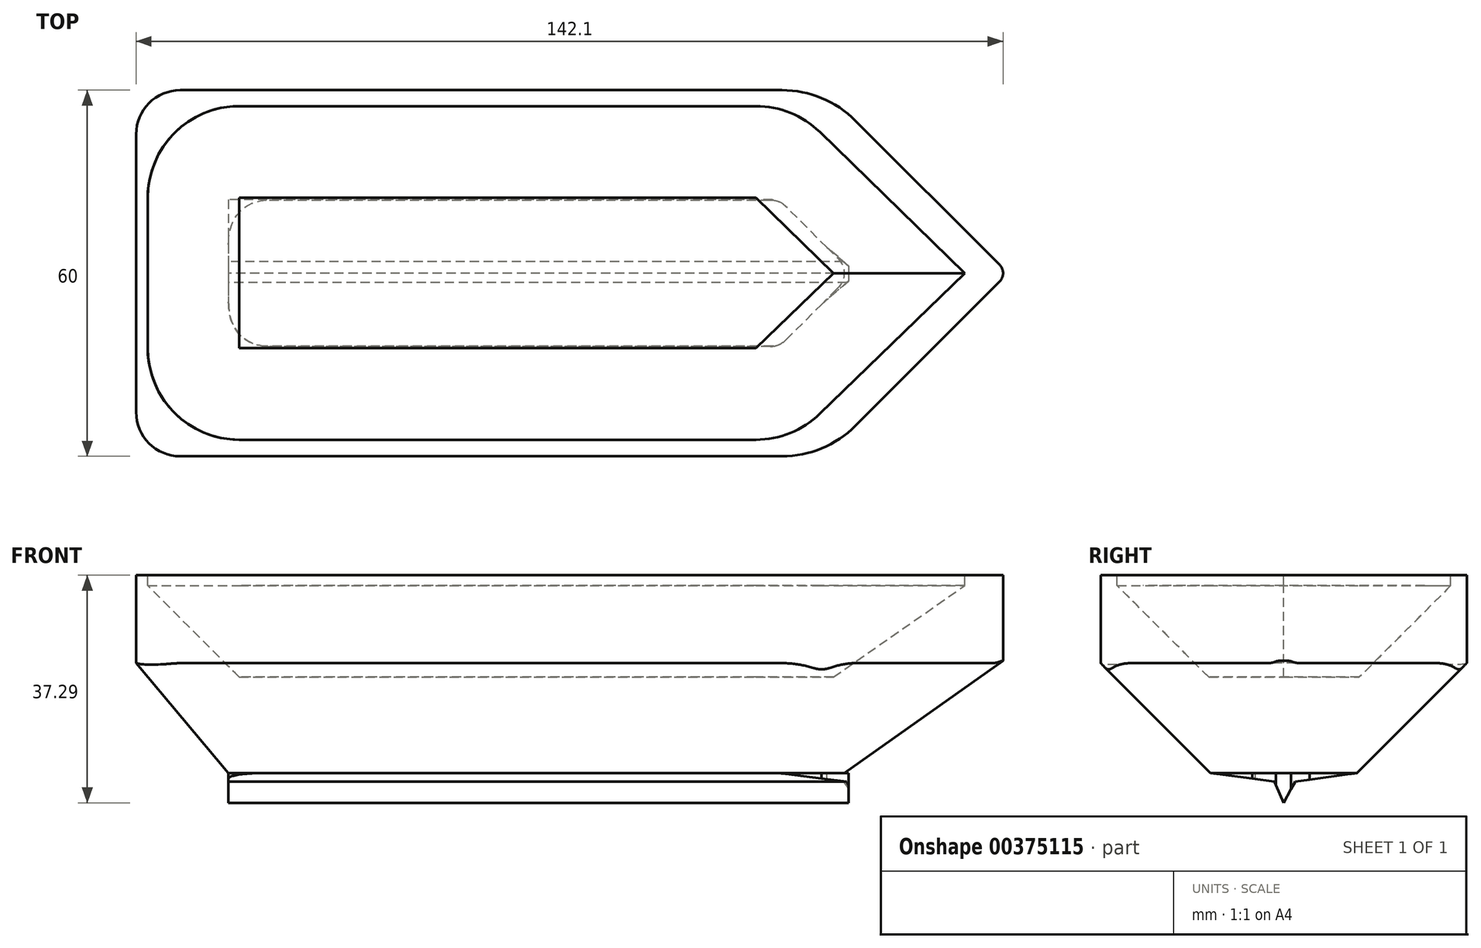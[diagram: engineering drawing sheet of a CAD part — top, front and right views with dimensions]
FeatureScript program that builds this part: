
annotation { "Feature Type Name" : "Feature", "Feature Type Description" : "" }
export const myFeature = defineFeature(function(context is Context, id is Id, definition is map)
    precondition{}
    {
        {
            var Q0;
            Q0=qCreatedBy(makeId("Top.planeOp"),FACE);
            var sketch = newSketch(context, id + "F0", { "sketchPlane" : qUnion([Q0])});
            skLineSegment(sketch, "E0", {"start": v(-55.59, 0) * mm, "end": v(-55.59, 30) * mm});
            skLineSegment(sketch, "E1", {"start": v(-55.59, 30) * mm, "end": v(-55.59, -30) * mm});
            skLineSegment(sketch, "E2", {"start": v(-55.59, -30) * mm, "end": v(87.31, -30) * mm});
            skLineSegment(sketch, "E3", {"start": v(87.31, -30) * mm, "end": v(87.31, 30) * mm});
            skLineSegment(sketch, "E4", {"start": v(87.31, 30) * mm, "end": v(-55.59, 30) * mm});
            skSolve(sketch);
        }
        {
            var Q0;
            {var subQ2=sQuery(id+"F0.wireOp",EDGE,"E2");Q0=makeQuery(id+"F0.imprint","IMPRINT",FACE,{"disambiguationData":[TD([[makeQuery(id+"F0.imprint","IMPRINT",EDGE,{"derivedFrom":subQ2}),1.0]])]});}
            extrude(context, id + "F1", {"entities" : qUnion([Q0]), "depth" : 32.4 * mm});
        }
        {
            var Q0;
            Q0=makeQuery(id+"F1.opExtrude","SWEPT_EDGE",EDGE,{"disambiguationData":[OSD([sQuery(id+"F0.wireOp",EDGE,"E2"),sQuery(id+"F0.wireOp",EDGE,"E3")])]});
            var Q1;
            Q1=makeQuery(id+"F1.opExtrude","SWEPT_EDGE",EDGE,{"disambiguationData":[OSD([sQuery(id+"F0.wireOp",EDGE,"E3"),sQuery(id+"F0.wireOp",EDGE,"E4")])]});
            chamfer(context, id + "F2", {"entities" : qUnion([Q0, Q1]), "width" : 30 * mm, "tangentPropagation" : true});
        }
        {
            var Q0;
            Q0=makeQuery(id+"F1.opExtrude","CAP_EDGE",EDGE,{"disambiguationData":[OSD([sQuery(id+"F0.wireOp",EDGE,"E2")])],"isStart":true});
            var Q1;
            Q1=makeQuery(id+"F1.opExtrude","CAP_EDGE",EDGE,{"disambiguationData":[OSD([sQuery(id+"F0.wireOp",EDGE,"E4")])],"isStart":true});
            var Q2;
            {var subQ0=sQuery(id+"F0.wireOp",EDGE,"E4");var subQ1=sQuery(id+"F0.wireOp",EDGE,"E3");Q2=makeQuery(id+"F2.opChamfer","BLEND_EDGE",EDGE,{"blendedFrom":[makeQuery(id+"F1.opExtrude","SWEPT_EDGE",EDGE,{"disambiguationData":[OSD([subQ1,subQ0])]}),makeQuery(id+"F1.opExtrude","CAP_FACE",FACE,{"disambiguationData":[OSD([sQuery(id+"F0.wireOp",EDGE,"E1"),sQuery(id+"F0.wireOp",EDGE,"E2"),subQ1,subQ0])],"isStart":true})],"blendedInto":[makeQuery(id+"F1.opExtrude","CAP_FACE",FACE,{"disambiguationData":[OSD([sQuery(id+"F0.wireOp",EDGE,"E1"),sQuery(id+"F0.wireOp",EDGE,"E2"),subQ1,subQ0])],"isStart":true})]});}
            var Q3;
            {var subQ0=sQuery(id+"F0.wireOp",EDGE,"E3");var subQ1=sQuery(id+"F0.wireOp",EDGE,"E2");Q3=makeQuery(id+"F2.opChamfer","BLEND_EDGE",EDGE,{"blendedFrom":[makeQuery(id+"F1.opExtrude","SWEPT_EDGE",EDGE,{"disambiguationData":[OSD([subQ1,subQ0])]}),makeQuery(id+"F1.opExtrude","CAP_FACE",FACE,{"disambiguationData":[OSD([sQuery(id+"F0.wireOp",EDGE,"E1"),subQ1,subQ0,sQuery(id+"F0.wireOp",EDGE,"E4")])],"isStart":true})],"blendedInto":[makeQuery(id+"F1.opExtrude","CAP_FACE",FACE,{"disambiguationData":[OSD([sQuery(id+"F0.wireOp",EDGE,"E1"),subQ1,subQ0,sQuery(id+"F0.wireOp",EDGE,"E4")])],"isStart":true})]});}
            chamfer(context, id + "F3", {"entities" : qUnion([Q0, Q1, Q2, Q3]), "width" : 18 * mm, "tangentPropagation" : true});
        }
        {
            var Q0;
            Q0=makeQuery(id+"F1.opExtrude","CAP_FACE",FACE,{"disambiguationData":[OSD([sQuery(id+"F0.wireOp",EDGE,"E1"),sQuery(id+"F0.wireOp",EDGE,"E2"),sQuery(id+"F0.wireOp",EDGE,"E3"),sQuery(id+"F0.wireOp",EDGE,"E4")])],"isStart":false});
            var sketch = newSketch(context, id + "F4", { "sketchPlane" : qUnion([Q0])});
            skLineSegment(sketch, "E5", {"start": v(-53.68, -12.3) * mm, "end": v(-53.68, 12.39) * mm});
            skLineSegment(sketch, "E6", {"start": v(-38.68, 27.39) * mm, "end": v(46, 27.39) * mm});
            skLineSegment(sketch, "E7", {"start": v(56.46, 23.14) * mm, "end": v(80.22, 0) * mm});
            skLineSegment(sketch, "E8", {"start": v(80.22, 0) * mm, "end": v(56.46, -23.06) * mm});
            skLineSegment(sketch, "E9", {"start": v(46.01, -27.3) * mm, "end": v(-38.68, -27.3) * mm});
            skPoint(sketch, "E10.visualSharp", {"position": v(52.1, 27.39) * mm});
            skArc(sketch, "E10.filletArc", {"start": v(56.46, 23.14) * mm, "mid": v(51.64, 26.29) * mm, "end": v(46, 27.39) * mm});
            skPoint(sketch, "E11.visualSharp", {"position": v(52.1, -27.3) * mm});
            skArc(sketch, "E11.filletArc", {"start": v(46.01, -27.3) * mm, "mid": v(51.65, -26.2) * mm, "end": v(56.46, -23.06) * mm});
            skPoint(sketch, "E12.visualSharp", {"position": v(-53.68, 27.39) * mm});
            skArc(sketch, "E12.filletArc", {"start": v(-38.68, 27.39) * mm, "mid": v(-49.29, 23) * mm, "end": v(-53.68, 12.39) * mm});
            skPoint(sketch, "E13.visualSharp", {"position": v(-53.68, -27.3) * mm});
            skArc(sketch, "E13.filletArc", {"start": v(-53.68, -12.3) * mm, "mid": v(-49.29, -22.9) * mm, "end": v(-38.68, -27.3) * mm});
            skSolve(sketch);
        }
        {
            var Q0;
            Q0=makeQuery(id+"F4.imprint","IMPRINT",FACE,{"disambiguationData":[TD([[makeQuery(id+"F4.imprint","IMPRINT",EDGE,{"derivedFrom":sQuery(id+"F4.wireOp",EDGE,"E5")}),-1.0]])]});
            extrude(context, id + "F5", {"entities" : qUnion([Q0]), "operationType" : NewBodyOperationType.REMOVE, "oppositeDirection" : true, "depth" : 16.7 * mm});
        }
        {
            var Q0;
            Q0=makeQuery(id+"F1.opExtrude","SWEPT_FACE",FACE,{"disambiguationData":[OSD([sQuery(id+"F0.wireOp",EDGE,"E2")])]});
            var sketch = newSketch(context, id + "F6", { "sketchPlane" : qUnion([Q0])});
            skLineSegment(sketch, "E14", {"start": v(-55.59, 18) * mm, "end": v(-55.59, 0) * mm});
            skLineSegment(sketch, "E15", {"start": v(-55.59, 0) * mm, "end": v(-40.45, 0) * mm});
            skLineSegment(sketch, "E16", {"start": v(-40.45, 0) * mm, "end": v(-55.59, 18) * mm});
            skSolve(sketch);
        }
        {
            var Q0;
            Q0=makeQuery(id+"F6.imprint","IMPRINT",FACE,{"disambiguationData":[TD([[makeQuery(id+"F6.imprint","IMPRINT",EDGE,{"derivedFrom":sQuery(id+"F6.wireOp",EDGE,"E14")}),1.0]])]});
            extrude(context, id + "F7", {"entities" : qUnion([Q0]), "operationType" : NewBodyOperationType.REMOVE, "oppositeDirection" : true, "depth" : 70.2 * mm});
        }
        {
            var Q0;
            Q0=makeQuery(id+"F1.opExtrude","SWEPT_FACE",FACE,{"disambiguationData":[OSD([sQuery(id+"F0.wireOp",EDGE,"E1")])]});
            var sketch = newSketch(context, id + "F8", { "sketchPlane" : qUnion([Q0])});
            skLineSegment(sketch, "E17", {"start": v(-12.03, 0) * mm, "end": v(-1.9, -1.4) * mm});
            skLineSegment(sketch, "E18", {"start": v(-1.9, -1.4) * mm, "end": v(0, -4.9) * mm});
            skLineSegment(sketch, "E19", {"start": v(0, -4.9) * mm, "end": v(1.53, -1.4) * mm});
            skLineSegment(sketch, "E20", {"start": v(1.53, -1.4) * mm, "end": v(11.97, 0) * mm});
            skLineSegment(sketch, "E21", {"start": v(-12.03, 0) * mm, "end": v(11.97, 0) * mm});
            skSolve(sketch);
        }
        {
            var Q0;
            Q0=makeQuery(id+"F8.imprint","IMPRINT",FACE,{"disambiguationData":[TD([[makeQuery(id+"F8.imprint","IMPRINT",EDGE,{"derivedFrom":sQuery(id+"F8.wireOp",EDGE,"E17")}),1.0]])]});
            extrude(context, id + "F9", {"entities" : qUnion([Q0]), "operationType" : NewBodyOperationType.ADD, "oppositeDirection" : true, "depth" : 116.8 * mm});
        }
        {
            var Q0;
            Q0 = qSketchRegion(id + "F8", true);
            var Q1;
            Q1=makeQuery(id+"F9.opExtrude","CAP_FACE",FACE,{"disambiguationData":[OSD([sQuery(id+"F8.wireOp",EDGE,"E17"),sQuery(id+"F8.wireOp",EDGE,"E18"),sQuery(id+"F8.wireOp",EDGE,"E19"),sQuery(id+"F8.wireOp",EDGE,"E20"),sQuery(id+"F8.wireOp",EDGE,"E21")])],"isStart":true});
            extrude(context, id + "F10", {"entities" : qUnion([Q0, Q1]), "operationType" : NewBodyOperationType.REMOVE, "oppositeDirection" : true, "depth" : 15.12 * mm});
        }
        {
            var Q0;
            Q0=makeQuery(id+"F1.opExtrude","SWEPT_EDGE",EDGE,{"disambiguationData":[OSD([sQuery(id+"F0.wireOp",EDGE,"E1"),sQuery(id+"F0.wireOp",EDGE,"E4")])]});
            var Q1;
            Q1=makeQuery(id+"F1.opExtrude","SWEPT_EDGE",EDGE,{"disambiguationData":[OSD([sQuery(id+"F0.wireOp",EDGE,"E1"),sQuery(id+"F0.wireOp",EDGE,"E2")])]});
            fillet(context, id + "F11", {"entities" : qUnion([Q0, Q1]), "radius" : 7.24 * mm, "tangentPropagation" : true, "allowEdgeOverflow" : false});
        }
        {
            var Q0;
            Q0=makeQuery(id+"F7.boolean.opBoolean","INTERSECT",EDGE,{"derivedFrom":[makeQuery(id+"F3.opChamfer","BLEND_FACE",FACE,{"disambiguationData":[OSD([sQuery(id+"F0.wireOp",EDGE,"E4")])]}),makeQuery(id+"F7.opExtrude","SWEPT_FACE",FACE,{"disambiguationData":[OSD([sQuery(id+"F6.wireOp",EDGE,"E16")])]})]});
            var Q1;
            Q1=makeQuery(id+"F7.boolean.opBoolean","INTERSECT",EDGE,{"derivedFrom":[makeQuery(id+"F3.opChamfer","BLEND_FACE",FACE,{"disambiguationData":[OSD([sQuery(id+"F0.wireOp",EDGE,"E2")])]}),makeQuery(id+"F7.opExtrude","SWEPT_FACE",FACE,{"disambiguationData":[OSD([sQuery(id+"F6.wireOp",EDGE,"E16")])]})]});
            fillet(context, id + "F12", {"entities" : qUnion([Q0, Q1]), "radius" : 9.46 * mm, "tangentPropagation" : true, "allowEdgeOverflow" : false});
        }
        {
            var Q0;
            {var subQ0=sQuery(id+"F0.wireOp",EDGE,"E3");Q0=makeQuery(id+"F2.opChamfer","BLEND_EDGE",EDGE,{"blendedFrom":[makeQuery(id+"F1.opExtrude","SWEPT_EDGE",EDGE,{"disambiguationData":[OSD([sQuery(id+"F0.wireOp",EDGE,"E2"),subQ0])]}),makeQuery(id+"F1.opExtrude","SWEPT_EDGE",EDGE,{"disambiguationData":[OSD([subQ0,sQuery(id+"F0.wireOp",EDGE,"E4")])]})],"blendedInto":[]});}
            fillet(context, id + "F13", {"entities" : qUnion([Q0]), "radius" : 1.93 * mm, "tangentPropagation" : true, "allowEdgeOverflow" : false});
        }
        {
            var Q0;
            {var subQ0=sQuery(id+"F0.wireOp",EDGE,"E2");Q0=makeQuery(id+"F2.opChamfer","BLEND_EDGE",EDGE,{"blendedFrom":[makeQuery(id+"F1.opExtrude","SWEPT_EDGE",EDGE,{"disambiguationData":[OSD([subQ0,sQuery(id+"F0.wireOp",EDGE,"E3")])]}),makeQuery(id+"F1.opExtrude","SWEPT_FACE",FACE,{"disambiguationData":[OSD([subQ0])]})],"blendedInto":[makeQuery(id+"F1.opExtrude","SWEPT_FACE",FACE,{"disambiguationData":[OSD([subQ0])]})]});}
            var Q1;
            {var subQ0=sQuery(id+"F0.wireOp",EDGE,"E4");Q1=makeQuery(id+"F2.opChamfer","BLEND_EDGE",EDGE,{"blendedFrom":[makeQuery(id+"F1.opExtrude","SWEPT_EDGE",EDGE,{"disambiguationData":[OSD([sQuery(id+"F0.wireOp",EDGE,"E3"),subQ0])]}),makeQuery(id+"F1.opExtrude","SWEPT_FACE",FACE,{"disambiguationData":[OSD([subQ0])]})],"blendedInto":[makeQuery(id+"F1.opExtrude","SWEPT_FACE",FACE,{"disambiguationData":[OSD([subQ0])]})]});}
            fillet(context, id + "F14", {"entities" : qUnion([Q0, Q1]), "radius" : 17 * mm, "tangentPropagation" : true, "allowEdgeOverflow" : false});
        }
        {
            var Q0;
            {var subQ0=sQuery(id+"F0.wireOp",EDGE,"E2");var subQ1=sQuery(id+"F0.wireOp",EDGE,"E3");Q0=makeQuery(id+"F3.opChamfer","BLEND_EDGE",EDGE,{"blendedFrom":[makeQuery(id+"F2.opChamfer","BLEND_EDGE",EDGE,{"blendedFrom":[makeQuery(id+"F1.opExtrude","SWEPT_EDGE",EDGE,{"disambiguationData":[OSD([subQ0,subQ1])]}),makeQuery(id+"F1.opExtrude","CAP_FACE",FACE,{"disambiguationData":[OSD([sQuery(id+"F0.wireOp",EDGE,"E1"),subQ0,subQ1,sQuery(id+"F0.wireOp",EDGE,"E4")])],"isStart":true})],"blendedInto":[makeQuery(id+"F1.opExtrude","CAP_FACE",FACE,{"disambiguationData":[OSD([sQuery(id+"F0.wireOp",EDGE,"E1"),subQ0,subQ1,sQuery(id+"F0.wireOp",EDGE,"E4")])],"isStart":true})]}),makeQuery(id+"F1.opExtrude","CAP_EDGE",EDGE,{"disambiguationData":[OSD([subQ0])],"isStart":true})],"blendedInto":[]});}
            var Q1;
            {var subQ0=sQuery(id+"F0.wireOp",EDGE,"E4");var subQ1=sQuery(id+"F0.wireOp",EDGE,"E3");var subQ2=sQuery(id+"F0.wireOp",EDGE,"E2");var subQ3=makeQuery(id+"F1.opExtrude","CAP_FACE",FACE,{"disambiguationData":[OSD([sQuery(id+"F0.wireOp",EDGE,"E1"),subQ2,subQ1,subQ0])],"isStart":true});Q1=makeQuery(id+"F3.opChamfer","BLEND_EDGE",EDGE,{"blendedFrom":[makeQuery(id+"F2.opChamfer","BLEND_EDGE",EDGE,{"blendedFrom":[makeQuery(id+"F1.opExtrude","SWEPT_EDGE",EDGE,{"disambiguationData":[OSD([subQ2,subQ1])]}),subQ3],"blendedInto":[subQ3]}),makeQuery(id+"F2.opChamfer","BLEND_EDGE",EDGE,{"blendedFrom":[makeQuery(id+"F1.opExtrude","SWEPT_EDGE",EDGE,{"disambiguationData":[OSD([subQ1,subQ0])]}),subQ3],"blendedInto":[subQ3]})],"blendedInto":[]});}
            var Q2;
            {var subQ0=sQuery(id+"F0.wireOp",EDGE,"E4");var subQ1=sQuery(id+"F0.wireOp",EDGE,"E3");Q2=makeQuery(id+"F3.opChamfer","BLEND_EDGE",EDGE,{"blendedFrom":[makeQuery(id+"F2.opChamfer","BLEND_EDGE",EDGE,{"blendedFrom":[makeQuery(id+"F1.opExtrude","SWEPT_EDGE",EDGE,{"disambiguationData":[OSD([subQ1,subQ0])]}),makeQuery(id+"F1.opExtrude","CAP_FACE",FACE,{"disambiguationData":[OSD([sQuery(id+"F0.wireOp",EDGE,"E1"),sQuery(id+"F0.wireOp",EDGE,"E2"),subQ1,subQ0])],"isStart":true})],"blendedInto":[makeQuery(id+"F1.opExtrude","CAP_FACE",FACE,{"disambiguationData":[OSD([sQuery(id+"F0.wireOp",EDGE,"E1"),sQuery(id+"F0.wireOp",EDGE,"E2"),subQ1,subQ0])],"isStart":true})]}),makeQuery(id+"F1.opExtrude","CAP_EDGE",EDGE,{"disambiguationData":[OSD([subQ0])],"isStart":true})],"blendedInto":[]});}
            fillet(context, id + "F15", {"entities" : qUnion([Q0, Q1, Q2]), "radius" : 5.16 * mm, "tangentPropagation" : true, "allowEdgeOverflow" : false});
        }
        {
            var Q0;
            Q0=makeQuery(id+"F5.boolean.opBoolean","COPY",EDGE,{"derivedFrom":makeQuery(id+"F5.opExtrude","CAP_EDGE",EDGE,{"disambiguationData":[OSD([sQuery(id+"F4.wireOp",EDGE,"E6")])],"isStart":false})});
            var Q1;
            Q1=makeQuery(id+"F5.boolean.opBoolean","COPY",EDGE,{"derivedFrom":makeQuery(id+"F5.opExtrude","CAP_EDGE",EDGE,{"disambiguationData":[OSD([sQuery(id+"F4.wireOp",EDGE,"E9")])],"isStart":false})});
            chamfer(context, id + "F16", {"entities" : qUnion([Q0, Q1]), "width" : 15 * mm, "tangentPropagation" : true});
        }
        {
            var Q0;
            Q0=makeQuery(id+"F5.boolean.opBoolean","COPY",FACE,{"derivedFrom":makeQuery(id+"F5.opExtrude","SWEPT_FACE",FACE,{"disambiguationData":[OSD([sQuery(id+"F4.wireOp",EDGE,"E6")])]})});
            var sketch = newSketch(context, id + "F17", { "sketchPlane" : qUnion([Q0])});
            skLineSegment(sketch, "E22", {"start": v(7.3, 30.7) * mm, "end": v(7.3, 28.24) * mm});
            skLineSegment(sketch, "E23", {"start": v(7.3, 28.24) * mm, "end": v(21.1, 28.24) * mm});
            skLineSegment(sketch, "E24", {"start": v(21.1, 28.24) * mm, "end": v(21.1, 30.7) * mm});
            skLineSegment(sketch, "E25", {"start": v(21.1, 30.7) * mm, "end": v(7.3, 30.7) * mm});
            skSolve(sketch);
        }
        {
            var Q0;
            Q0=sQuery(id+"F17.wireOp",EDGE,"E23");
            var Q1;
            Q1=sQuery(id+"F17.wireOp",EDGE,"E22");
            var Q2;
            Q2=sQuery(id+"F17.wireOp",EDGE,"E25");
            var Q3;
            Q3=sQuery(id+"F17.wireOp",EDGE,"E24");
            extrude(context, id + "F18", {"bodyType" : ToolBodyType.SURFACE, "surfaceEntities" : qUnion([Q0, Q1, Q2, Q3]), "depth" : 56.9 * mm});
        }
        {
            var Q0;
            {var subQ0=sQuery(id+"F0.wireOp",EDGE,"E4");var subQ1=sQuery(id+"F8.wireOp",EDGE,"E21");Q0=makeQuery(id+"F9.boolean.opBoolean","SPLIT",FACE,{"disambiguationData":[TD([makeQuery(id+"F3.opChamfer","BLEND_FACE",FACE,{"disambiguationData":[OSD([subQ0])]})])],"derivedFrom":makeQuery(id+"F9.opExtrude","SWEPT_FACE",FACE,{"disambiguationData":[OSD([subQ1])]})});}
            var sketch = newSketch(context, id + "F19", { "sketchPlane" : qUnion([Q0])});
            skLineSegment(sketch, "E26", {"start": v(-40.45, -4.71) * mm, "end": v(-34.38, -11.97) * mm});
            skLineSegment(sketch, "E27", {"start": v(-40.45, -4.71) * mm, "end": v(-40.77, -4.71) * mm});
            skLineSegment(sketch, "E28", {"start": v(-40.77, -4.71) * mm, "end": v(-41.05, -12.58) * mm});
            skLineSegment(sketch, "E29", {"start": v(-41.05, -12.58) * mm, "end": v(-34.38, -12.34) * mm});
            skLineSegment(sketch, "E30", {"start": v(-34.38, -12.34) * mm, "end": v(-34.46, -12.34) * mm});
            skLineSegment(sketch, "E31", {"start": v(-34.38, -11.97) * mm, "end": v(-34.38, -12.34) * mm});
            skSolve(sketch);
        }
        {
            var Q0;
            {var subQ1=sQuery(id+"F6.wireOp",EDGE,"E16");var subQ2=makeQuery(id+"F7.opExtrude","SWEPT_FACE",FACE,{"disambiguationData":[OSD([subQ1])]});var subQ3=makeQuery(id+"F7.boolean.opBoolean","COPY",FACE,{"derivedFrom":subQ2});var subQ4=sQuery(id+"F0.wireOp",EDGE,"E4");var subQ5=sQuery(id+"F8.wireOp",EDGE,"E21");var subQ6=sQuery(id+"F8.wireOp",EDGE,"E20");var subQ10=sQuery(id+"F0.wireOp",EDGE,"E3");var subQ11=sQuery(id+"F0.wireOp",EDGE,"E2");var subQ12=sQuery(id+"F0.wireOp",EDGE,"E1");var subQ13=makeQuery(id+"F1.opExtrude","CAP_FACE",FACE,{"disambiguationData":[OSD([subQ12,subQ11,subQ10,subQ4])],"isStart":true});var subQ15=makeQuery(id+"F9.opExtrude","SWEPT_FACE",FACE,{"disambiguationData":[OSD([subQ6])]});var subQ16=makeQuery(id+"F9.opExtrude","SWEPT_FACE",FACE,{"disambiguationData":[OSD([subQ5])]});var subQ20=makeQuery(id+"F9.opExtrude","SWEPT_EDGE",EDGE,{"disambiguationData":[OSD([subQ6,subQ5])]});var subQ21=makeQuery(id+"F12.opFillet","MERGE",EDGE,{"derivedFrom":[makeQuery(id+"F9.boolean.opBoolean","SPLIT",EDGE,{"disambiguationData":[topologyDisambiguationEdgeConnected([subQ13,subQ15])],"derivedFrom":subQ20}),makeQuery(id+"F9.boolean.opBoolean","SPLIT",EDGE,{"disambiguationData":[topologyDisambiguationEdgeConnected([subQ15,subQ16]),TD([subQ3])],"derivedFrom":subQ20})]});Q0=makeQuery(id+"F19.imprint","IMPRINT",FACE,{"disambiguationData":[TD([[makeQuery(id+"F19.imprint","IMPRINT",EDGE,{"derivedFrom":subQ21}),-1.0]])]});}
            var Q1;
            {var subQ10=sQuery(id+"F19.wireOp",EDGE,"E28");Q1=makeQuery(id+"F19.imprint","IMPRINT",FACE,{"disambiguationData":[TD([[makeQuery(id+"F19.imprint","IMPRINT",EDGE,{"derivedFrom":subQ10}),1.0]])]});}
            extrude(context, id + "F20", {"entities" : qUnion([Q0, Q1]), "operationType" : NewBodyOperationType.REMOVE, "oppositeDirection" : true, "depth" : 25 * mm});
        }
        {
            var Q0;
            {var subQ0=sQuery(id+"F0.wireOp",EDGE,"E4");var subQ1=sQuery(id+"F8.wireOp",EDGE,"E21");Q0=makeQuery(id+"F9.boolean.opBoolean","SPLIT",FACE,{"disambiguationData":[TD([makeQuery(id+"F3.opChamfer","BLEND_FACE",FACE,{"disambiguationData":[OSD([subQ0])]})])],"derivedFrom":makeQuery(id+"F9.opExtrude","SWEPT_FACE",FACE,{"disambiguationData":[OSD([subQ1])]})});}
            var sketch = newSketch(context, id + "F21", { "sketchPlane" : qUnion([Q0])});
            skLineSegment(sketch, "E32", {"start": v(-40.94, 12.21) * mm, "end": v(-40.45, 4.71) * mm});
            skLineSegment(sketch, "E33", {"start": v(-40.45, 4.71) * mm, "end": v(-33.71, 12) * mm});
            skLineSegment(sketch, "E34", {"start": v(-33.71, 12) * mm, "end": v(-40.94, 12.21) * mm});
            skSolve(sketch);
        }
        {
            var Q0;
            {var subQ0=sQuery(id+"F8.wireOp",EDGE,"E21");var subQ1=makeQuery(id+"F10.boolean.opBoolean","COPY",EDGE,{"derivedFrom":makeQuery(id+"F10.opExtrude","CAP_EDGE",EDGE,{"disambiguationData":[OSD([subQ0]),TDD([makeQuery(id+"F8.imprint","IMPRINT",EDGE,{"derivedFrom":subQ0})])],"isStart":false})});var subQ8=sQuery(id+"F21.wireOp",EDGE,"E32");var subQ23=makeQuery(id+"F21.imprint","INTERSECT",VERTEX,{"derivedFrom":[subQ1,subQ8]});Q0=makeQuery(id+"F21.imprint","IMPRINT",FACE,{"disambiguationData":[TD([[makeQuery(id+"F21.imprint","IMPRINT",EDGE,{"disambiguationData":[TD([[subQ23,1.0]])],"derivedFrom":subQ1}),1.0]])]});}
            var Q1;
            {var subQ0=sQuery(id+"F21.wireOp",EDGE,"E34");var subQ1=sQuery(id+"F21.wireOp",EDGE,"E32");var subQ2=makeQuery(id+"F21.imprint","INTERSECT",VERTEX,{"derivedFrom":[subQ1,subQ0]});Q1=makeQuery(id+"F21.imprint","IMPRINT",FACE,{"disambiguationData":[TD([[makeQuery(id+"F21.imprint","IMPRINT",EDGE,{"disambiguationData":[TD([[subQ2,-1.0]])],"derivedFrom":subQ1}),1.0]])]});}
            extrude(context, id + "F22", {"entities" : qUnion([Q0, Q1]), "operationType" : NewBodyOperationType.REMOVE, "oppositeDirection" : true, "depth" : 25 * mm});
        }
        {
            var Q0;
            {var subQ0=sQuery(id+"F0.wireOp",EDGE,"E2");var subQ1=sQuery(id+"F0.wireOp",EDGE,"E4");var subQ2=sQuery(id+"F0.wireOp",EDGE,"E3");var subQ3=sQuery(id+"F0.wireOp",EDGE,"E1");var subQ4=makeQuery(id+"F1.opExtrude","CAP_FACE",FACE,{"disambiguationData":[OSD([subQ3,subQ0,subQ2,subQ1])],"isStart":true});var subQ5=makeQuery(id+"F2.opChamfer","BLEND_EDGE",EDGE,{"blendedFrom":[makeQuery(id+"F1.opExtrude","SWEPT_EDGE",EDGE,{"disambiguationData":[OSD([subQ0,subQ2])]}),subQ4],"blendedInto":[subQ4]});var subQ13=makeQuery(id+"F3.opChamfer","BLEND_FACE",FACE,{"disambiguationData":[OSD([subQ3,subQ0,subQ2,subQ1]),TDD([subQ5])]});var subQ14=sQuery(id+"F8.wireOp",EDGE,"E21");var subQ18=makeQuery(id+"F3.opChamfer","BLEND_FACE",FACE,{"disambiguationData":[OSD([subQ1])]});var subQ19=makeQuery(id+"F9.opExtrude","SWEPT_FACE",FACE,{"disambiguationData":[OSD([subQ14])]});Q0=makeQuery(id+"F22.boolean.opBoolean","SPLIT",FACE,{"disambiguationData":[TD([subQ18])],"derivedFrom":makeQuery(id+"F15.opFillet","MERGE",FACE,{"derivedFrom":[makeQuery(id+"F9.boolean.opBoolean","SPLIT",FACE,{"disambiguationData":[TD([subQ13])],"derivedFrom":subQ19}),makeQuery(id+"F9.boolean.opBoolean","SPLIT",FACE,{"disambiguationData":[TD([subQ18])],"derivedFrom":subQ19})]})});}
            var sketch = newSketch(context, id + "F23", { "sketchPlane" : qUnion([Q0])});
            skLineSegment(sketch, "E35", {"start": v(48.35, 12) * mm, "end": v(62.68, 13.16) * mm});
            skLineSegment(sketch, "E36", {"start": v(62.68, 13.16) * mm, "end": v(62.68, -11.64) * mm});
            skLineSegment(sketch, "E37", {"start": v(62.68, -11.64) * mm, "end": v(62.68, -12.9) * mm});
            skLineSegment(sketch, "E38", {"start": v(62.68, -12.9) * mm, "end": v(48.79, -12.34) * mm});
            skLineSegment(sketch, "E39", {"start": v(48.79, -12.34) * mm, "end": v(48.79, -11.97) * mm});
            skLineSegment(sketch, "E40", {"start": v(48.79, -11.97) * mm, "end": v(62.68, 0) * mm});
            skPoint(sketch, "E40.endSnap0", {"position": v(60.47, 0) * mm});
            skLineSegment(sketch, "E41", {"start": v(62.68, 0) * mm, "end": v(48.35, 12) * mm});
            skSolve(sketch);
        }
        {
            var Q0;
            {var subQ0=sQuery(id+"F0.wireOp",EDGE,"E4");var subQ1=sQuery(id+"F0.wireOp",EDGE,"E3");var subQ2=sQuery(id+"F0.wireOp",EDGE,"E2");var subQ3=sQuery(id+"F0.wireOp",EDGE,"E1");var subQ4=makeQuery(id+"F1.opExtrude","CAP_FACE",FACE,{"disambiguationData":[OSD([subQ3,subQ2,subQ1,subQ0])],"isStart":true});var subQ5=sQuery(id+"F8.wireOp",EDGE,"E20");var subQ6=makeQuery(id+"F9.opExtrude","SWEPT_FACE",FACE,{"disambiguationData":[OSD([subQ5])]});var subQ7=sQuery(id+"F8.wireOp",EDGE,"E21");var subQ8=makeQuery(id+"F9.opExtrude","SWEPT_EDGE",EDGE,{"disambiguationData":[OSD([subQ5,subQ7])]});var subQ9=sQuery(id+"F8.wireOp",EDGE,"E19");var subQ10=sQuery(id+"F8.wireOp",EDGE,"E18");var subQ11=sQuery(id+"F8.wireOp",EDGE,"E17");var subQ12=makeQuery(id+"F9.opExtrude","CAP_FACE",FACE,{"disambiguationData":[OSD([subQ11,subQ10,subQ9,subQ5,subQ7])],"isStart":false});var subQ15=makeQuery(id+"F9.opExtrude","SWEPT_FACE",FACE,{"disambiguationData":[OSD([subQ7])]});var subQ16=makeQuery(id+"F15.opFillet","MERGE",EDGE,{"derivedFrom":[makeQuery(id+"F9.boolean.opBoolean","SPLIT",EDGE,{"disambiguationData":[topologyDisambiguationEdgeConnected([subQ6,subQ15]),TD([subQ12])],"derivedFrom":subQ8}),makeQuery(id+"F12.opFillet","SPLIT",EDGE,{"derivedFrom":makeQuery(id+"F9.boolean.opBoolean","SPLIT",EDGE,{"disambiguationData":[topologyDisambiguationEdgeConnected([subQ4,subQ6])],"derivedFrom":subQ8})})]});Q0=makeQuery(id+"F23.imprint","IMPRINT",FACE,{"disambiguationData":[TD([[makeQuery(id+"F23.imprint","IMPRINT",EDGE,{"derivedFrom":subQ16}),-1.0]])]});}
            extrude(context, id + "F24", {"entities" : qUnion([Q0]), "operationType" : NewBodyOperationType.REMOVE, "oppositeDirection" : true, "depth" : 25 * mm});
        }
        {
            var Q0;
            {var subQ16=sQuery(id+"F23.wireOp",EDGE,"E36");var subQ17=sQuery(id+"F23.wireOp",EDGE,"E35");var subQ18=makeQuery(id+"F23.imprint","INTERSECT",VERTEX,{"derivedFrom":[subQ17,subQ16]});Q0=makeQuery(id+"F23.imprint","IMPRINT",FACE,{"disambiguationData":[TD([[makeQuery(id+"F23.imprint","IMPRINT",EDGE,{"disambiguationData":[TD([[subQ18,1.0]])],"derivedFrom":subQ17}),-1.0]])]});}
            var Q1;
            {var subQ1=sQuery(id+"F8.wireOp",EDGE,"E21");var subQ5=sQuery(id+"F8.wireOp",EDGE,"E17");var subQ26=sQuery(id+"F23.wireOp",EDGE,"E35");var subQ27=makeQuery(id+"F9.opExtrude","SWEPT_EDGE",EDGE,{"disambiguationData":[OSD([subQ5,subQ1])]});var subQ28=makeQuery(id+"F23.imprint","INTERSECT",VERTEX,{"derivedFrom":[subQ27,subQ26]});Q1=makeQuery(id+"F23.imprint","IMPRINT",FACE,{"disambiguationData":[TD([[makeQuery(id+"F23.imprint","IMPRINT",EDGE,{"disambiguationData":[TD([[subQ28,1.0]])],"derivedFrom":subQ27}),1.0]])]});}
            extrude(context, id + "F25", {"entities" : qUnion([Q0, Q1]), "operationType" : NewBodyOperationType.REMOVE, "oppositeDirection" : true, "depth" : 25 * mm});
        }
    });
